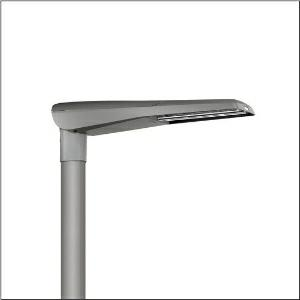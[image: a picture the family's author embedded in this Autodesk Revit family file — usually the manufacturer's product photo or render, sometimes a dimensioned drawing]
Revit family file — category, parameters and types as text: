
# Revit family: streetlight_sl_11_iq_mini___st0_5a_5xc2bc1f08ge_6b58
name_source: partatom
category: Lighting Fixtures
units: mm (PartAtom-declared; Revit-internal decimal feet)

## family parameters
Cut with Voids When Loaded = No
Host = Face
Light Source = No
Part Type = Normal
Room Calculation Point = No
Round Connector Dimension = Use Diameter
Shared = No

## types (1)
- --- (1 x LED, 3020 lm, 25.3 W, 2200K)
    Apparent Load = 25 VA
    CIE Flux Codes = 43 74 97 100 100
    Color Rendering = 70
    Color Temperature = 2200K
    Default Elevation = 1800 mm
    Description = Streetlight SL 11 iQ mini, mast luminaire, primary light control with 3 zone facetted reflector, of plastic, silver coated, highly specular, primary optical cover: cover, of PMMA, transparent, light distribution: ST0.5a, light emission: direct distribution, primary light characteristic: asymmetric, installation type: post-top, side-entry, lamps: LED, High Power LED, rated values: 3.550lm | 24,9W | 142,6lm/W (begin service life); end service life: 3.550lm | 25,7W; at 50% lumin. flux: 1.775lm | 12,8W | 138,7lm/W, colour temperature: 2200/2700/3000/4000K, colour rendering: CRI > 70, light colour: 722/727/730/740, light setting 1 begin service life: 100% | 3.550lm | 24,9W | 142,6lm/W | 3.000K, light setting 1 end service life: 25,7W, further light settings possible, control: Street-Remote, Auto-Match, Temp-Guard, Lumen-Switch, Night-Set, Smart-Wire, Light-Fading, Desk-Remote (wireless, voltage-free reading and setting of iQ features in the workshop via application-optimized NFC function/RFID function), optimised constant luminous flux control (CLO 2.0), with cable H07RN-F 3x 1.5mm², mains connection: 230..240V, AC, 50/60Hz, connection cable pre-assembled, cable length: 6,5m, luminaire housing, of diecast aluminium, powder-coated, SITECO metallic grey (DB 702S), please order mast flange separately, inclination adjustable without tools: 0°, 5°, 10°, 15° (post-top) | 0°, -5°, -10°, -15° (side-entry), sealing non-destructively replaceable, multi-level sealing system, length: 736mm, width: 174mm, height: 116mm, mast flange for spigot size: 42mm (side-entry): 5XC10008XM4, 60/48mm (side-entry/post-top): 5XC10108XM2, 76/60mm (side-entry/post-top): 5XC10108XM1, equipment: standard, protection rating (complete): IP66, insulation class (complete): insulation class II (safety insulation), certification: CE, ENEC, ENEC+, VDE, impact resistance: IK10, permissible operating ambient temperature for outdoor applications: -25..+50°C, standard-compliant lighting for roads and squares, Environmental Product Declaration (EPD) tested and certified by an independent institute, packaging unit: 1 piece

Light Distribution: ST0.5a
    Height = 116 mm
    Lamp = 1 x LED
    Lamp Light Flux = 3020 lm
    Lamp Power = 25.3 W
    Lamp count = 1
    Length = 736 mm
    Luminous efficacy = 119 lm/W
    Manufacturer = Siteco
    ModVariant = No
    Model = 5XC2BC1F08GE
    Number of Poles = 1
    OnlyDefault = Yes
    Power Factor = 1
    Product Name = Streetlight SL 11 iQ mini | ST0.5a
    Product group = mast luminaire | pylon top
    ProductGroupID = 6100
    Protection Class = Protection class II
    Protection Degree = IP 66
    RLX_Detail_Level = 1
    RLX_Emergency_Light_Flux = 0 lm
    RLX_Emergency_Type = 0
    RLX_Emergency_Type_DB = No
    RlxData = <blob elided: 58237 chars, md5=c3bfe905>
    Socket = socket
    Standby Power = 0 W
    System Light Flux = 3020 lm
    System Power = 25 W
    Type Comments = individual setting: luminous flux: 100 % | dim-lin: 254 | 351 mA
    Type Image = l_1003508.jpg
    URL = http://relux.com
    VarID = @adj_042927
    Voltage = 0 V
    Weight = 0.00 kg
    Width = 174 mm

## geometry (parser evidence)
native form markers: Blend x4, Sweep x10
no freeform markers — native parametric forms only
